# Revit family: Hager-Vega_D-IP40-syst-BE-en
name_source: partatom
category: Electrical Equipment
units: mm (PartAtom-declared; Revit-internal decimal feet)

## family parameters
Cut with Voids When Loaded = No
Host = Face
Panel Configuration = Two Columns, Circuits Across
Part Type = Panelboard
Room Calculation Point = No
Round Connector Dimension = Use Diameter
Shared = No

## types (12) — shared parameters
EF000003 - Mounting method = EV000383 - Flush mounted (plaster)
EF000007 - Colour = EV000202 - White
EF000008 - Width = 600 mm
EF000049 - Depth = 150 mm  [stored 0.492126 ft]
EF000116 - RAL-number = 9010
EF000118 - With mounting plate = No
EF000218 - Built-in depth = 150 mm  [stored 0.492126 ft]
EF000339 - Type of cover = EV004216 - Door
EF000846 - Built-in width = 550 mm
EF001062 - EMC-version = No
EF001088 - Extension possible = Yes
EF001131 - Internal depth = 110 mm
EF001134 - DIN-rail = Yes
EF001596 - Material housing = EV000154 - Other
EF002950 - Width in number of modular spacings = 24
EF005474 - Degree of protection (IP) = EV006415 - IP40
EF006306 - With lock = No
EF015776 - Earthing terminal block = No
EF015777 - Neutral terminal block = No
EF015941 - Signal passing door = No
HG000001 - Number of columns = 1
HG000002 - With door or cover = Yes
HG000003 - Range = Vega D
HG000005 - Thickness = 3 mm  [stored 0.00984252 ft]
HG000006 - Flush mounted = Yes
HG000009 - Double swing door = No
HG000010 - Asymmetric doors = No
HG000011 - Empty rows from bottom = No
HG000017 - Distance between poles = 18 mm  [stored 0.0590551 ft]
Manufacturer = Hager
Type Comments = Vega D
zero-valued in all types: Default Elevation, HG000007 - Number of empty columns, HG000008 - Number of empty rows

## per-type parameters (varying)
| type | EF000040 - Height | EF000266 - Number of rows | EF000332 - Built-in height | EF006244 - Transparent cover/door | EF009212 - Cover model | HG000004 - Manufacturer reference | Model |
| Recessed mounted IP40 W600 H1137 D150 24 Modular spacings - FU62BN | 1137 mm | 6 | 1137 mm | No | EV000116 - Closed | FU62BN | FU62BN |
| Recessed mounted IP40 W600 H1137 D150 24 Modular spacings - FU62CN | 1137 mm | 6 | 1137 mm | Yes | EV009916 - With notch | FU62CN | FU62CN |
| Recessed mounted IP40 W600 H1287 D150 24 Modular spacings - FU72BN | 1287 mm | 7 | 1287 mm | No | EV000116 - Closed | FU72BN | FU72BN |
| Recessed mounted IP40 W600 H1287 D150 24 Modular spacings - FU72CN | 1287 mm | 7 | 1287 mm | Yes | EV009916 - With notch | FU72CN | FU72CN |
| Recessed mounted IP40 W600 H537 D150 24 Modular spacings - FU22BN | 537 mm | 2 | 537 mm | No | EV000116 - Closed | FU22BN | FU22BN |
| Recessed mounted IP40 W600 H537 D150 24 Modular spacings - FU22CN | 537 mm | 2 | 537 mm | Yes | EV009916 - With notch | FU22CN | FU22CN |
| Recessed mounted IP40 W600 H687 D150 24 Modular spacings - FU32BN | 687 mm | 3 | 687 mm | No | EV000116 - Closed | FU32BN | FU32BN |
| Recessed mounted IP40 W600 H687 D150 24 Modular spacings - FU32CN | 687 mm | 3 | 687 mm | Yes | EV009916 - With notch | FU32CN | FU32CN |
| Recessed mounted IP40 W600 H837 D150 24 Modular spacings - FU42BN | 837 mm | 4 | 837 mm | No | EV000116 - Closed | FU42BN | FU42BN |
| Recessed mounted IP40 W600 H837 D150 24 Modular spacings - FU42CN | 837 mm | 4 | 837 mm | Yes | EV009916 - With notch | FU42CN | FU42CN |
| Recessed mounted IP40 W600 H987 D150 24 Modular spacings - FU52BN | 987 mm  [stored 3.23819 ft] | 5 | 987 mm  [stored 3.23819 ft] | No | EV000116 - Closed | FU52BN | FU52BN |
| Recessed mounted IP40 W600 H987 D150 24 Modular spacings - FU52CN | 987 mm  [stored 3.23819 ft] | 5 | 987 mm  [stored 3.23819 ft] | Yes | EV009916 - With notch | FU52CN | FU52CN |

note: [stored X ft] marks values corroborated as IEEE doubles in the binary element streams (Revit-internal decimal feet)

## geometry (parser evidence)
native form markers: Sweep x17
no freeform markers — native parametric forms only
